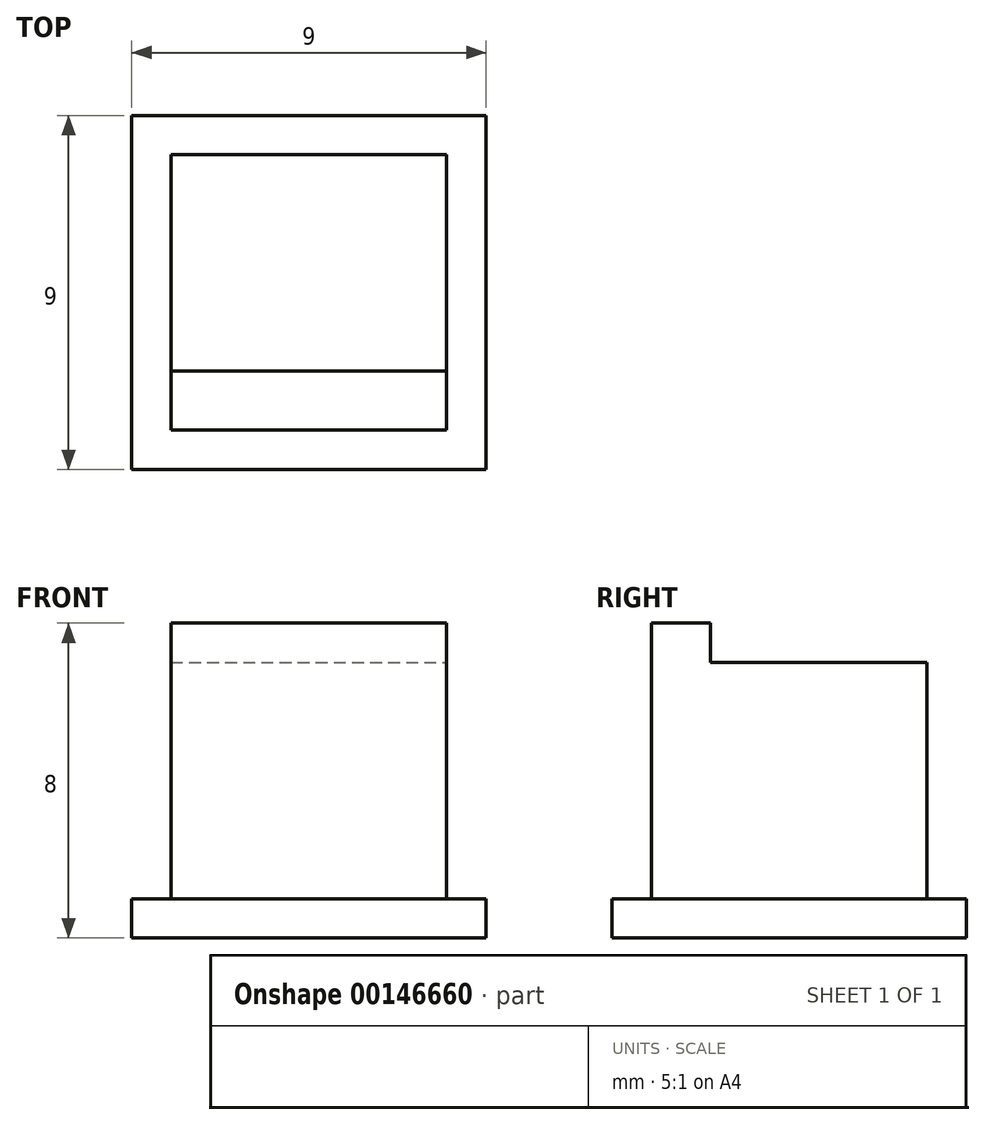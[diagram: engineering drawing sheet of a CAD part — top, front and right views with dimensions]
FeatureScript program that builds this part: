
annotation { "Feature Type Name" : "Feature", "Feature Type Description" : "" }
export const myFeature = defineFeature(function(context is Context, id is Id, definition is map)
    precondition{}
    {
        {
            var Q0;
            Q0=qCreatedBy(makeId("Top.planeOp"),FACE);
            var sketch = newSketch(context, id + "F0", { "sketchPlane" : qUnion([Q0])});
            skLineSegment(sketch, "E0.bottom", {"start": v(-11.48, 11.26) * mm, "end": v(-4.48, 11.26) * mm});
            skLineSegment(sketch, "E0.top", {"start": v(-11.48, 4.26) * mm, "end": v(-4.48, 4.26) * mm});
            skLineSegment(sketch, "E0.left", {"start": v(-11.48, 11.26) * mm, "end": v(-11.48, 4.26) * mm});
            skLineSegment(sketch, "E0.right", {"start": v(-4.48, 11.26) * mm, "end": v(-4.48, 4.26) * mm});
            skSolve(sketch);
        }
        {
            var Q0;
            Q0=makeQuery(id+"F0.imprint","IMPRINT",FACE,{"disambiguationData":[TD([[makeQuery(id+"F0.imprint","IMPRINT",EDGE,{"derivedFrom":sQuery(id+"F0.wireOp",EDGE,"E0.bottom")}),-1.0]])]});
            extrude(context, id + "F1", {"entities" : qUnion([Q0]), "depth" : 6 * mm});
        }
        {
            var Q0;
            Q0=makeQuery(id+"F1.opExtrude","CAP_FACE",FACE,{"disambiguationData":[OSD([sQuery(id+"F0.wireOp",EDGE,"E0.bottom"),sQuery(id+"F0.wireOp",EDGE,"E0.top"),sQuery(id+"F0.wireOp",EDGE,"E0.left"),sQuery(id+"F0.wireOp",EDGE,"E0.right")])],"isStart":true});
            var sketch = newSketch(context, id + "F2", { "sketchPlane" : qUnion([Q0])});
            skLineSegment(sketch, "E1.bottom", {"start": v(-12.48, -3.26) * mm, "end": v(-3.48, -3.26) * mm});
            skLineSegment(sketch, "E1.top", {"start": v(-12.48, -12.26) * mm, "end": v(-3.48, -12.26) * mm});
            skLineSegment(sketch, "E1.left", {"start": v(-12.48, -3.26) * mm, "end": v(-12.48, -12.26) * mm});
            skLineSegment(sketch, "E1.right", {"start": v(-3.48, -3.26) * mm, "end": v(-3.48, -12.26) * mm});
            skLineSegment(sketch, "E2", {"start": v(-11.48, -4.26) * mm, "end": v(-11.48, -3.26) * mm, "construction": true});
            skLineSegment(sketch, "E3", {"start": v(-11.48, -4.26) * mm, "end": v(-12.48, -4.26) * mm, "construction": true});
            skSolve(sketch);
        }
        {
            var Q0;
            Q0=makeQuery(id+"F2.imprint","IMPRINT",FACE,{"disambiguationData":[TD([[makeQuery(id+"F2.imprint","IMPRINT",EDGE,{"derivedFrom":makeQuery(id+"F1.opExtrude","CAP_EDGE",EDGE,{"disambiguationData":[OSD([sQuery(id+"F0.wireOp",EDGE,"E0.bottom")])],"isStart":true})}),1.0]])]});
            var Q1;
            Q1=makeQuery(id+"F2.imprint","IMPRINT",FACE,{"disambiguationData":[TD([[makeQuery(id+"F2.imprint","IMPRINT",EDGE,{"derivedFrom":sQuery(id+"F2.wireOp",EDGE,"E1.bottom")}),-1.0]])]});
            extrude(context, id + "F3", {"entities" : qUnion([Q0, Q1]), "operationType" : NewBodyOperationType.ADD, "depth" : 1 * mm});
        }
        {
            var Q0;
            Q0=makeQuery(id+"F1.opExtrude","CAP_FACE",FACE,{"disambiguationData":[OSD([sQuery(id+"F0.wireOp",EDGE,"E0.bottom"),sQuery(id+"F0.wireOp",EDGE,"E0.top"),sQuery(id+"F0.wireOp",EDGE,"E0.left"),sQuery(id+"F0.wireOp",EDGE,"E0.right")])],"isStart":false});
            var sketch = newSketch(context, id + "F4", { "sketchPlane" : qUnion([Q0])});
            skLineSegment(sketch, "E4.bottom", {"start": v(-4.48, 4.26) * mm, "end": v(-11.48, 4.26) * mm});
            skLineSegment(sketch, "E4.top", {"start": v(-4.48, 5.76) * mm, "end": v(-11.48, 5.76) * mm});
            skLineSegment(sketch, "E4.left", {"start": v(-4.48, 4.26) * mm, "end": v(-4.48, 5.76) * mm});
            skLineSegment(sketch, "E4.right", {"start": v(-11.48, 4.26) * mm, "end": v(-11.48, 5.76) * mm});
            skSolve(sketch);
        }
        {
            var Q0;
            Q0=makeQuery(id+"F4.imprint","IMPRINT",FACE,{"disambiguationData":[TD([[makeQuery(id+"F4.imprint","IMPRINT",EDGE,{"derivedFrom":sQuery(id+"F4.wireOp",EDGE,"E4.bottom")}),1.0]])]});
            extrude(context, id + "F5", {"entities" : qUnion([Q0]), "operationType" : NewBodyOperationType.ADD, "depth" : 1 * mm});
        }
    });
